# Revit family: STL22465BR_30_STL22465PTO_30
name_source: partatom
category: Luminárias
units: mm (PartAtom-declared; Revit-internal decimal feet)

## family parameters
Com base no plano de trabalho = Não
Compartilhado = Não
Corte com vazios quando carregada = Não
Cota do conector redondo = Utilizar diâmetro
Fonte luminosa = Sim
Manter orientação da anotação = Não
Ponto de cálculo do ambiente = Não
Sempre na vertical = Sim
Tipo de parte = Normal

## types (2) — shared parameters
Altura = 0.05 m
Comprimento = 0.19 m
Cromado = Cromado
Fabricante = Stella
Filtro de cor = 16777215
Fluxo Luminoso = 420 lm
Grau de proteção (IP) = IP20
IRC (Índice de reprodução de cores) = >93 (R9>60)
Largura = 0.04 m
Luminoso = Luminoso - 3000K
Modelo = Trace - Luminária de Luz Pontual
Potência máxima = 7 W
Temperatura da cor (K) = 3000 K
Tensão Elétrica = 100V-240V
Troca de temperatura da cor de lâmpada com esmaecimento = <Nenhum>
URL = https://stella.com.br
Ângulo de Abertura = 40°
Ângulo de inclinação = 90.00°
zero-valued in all types: Elevação padrão

## per-type parameters (varying)
| type | Arquivo de rede fotométrica | Estrutura | Parafuso Branco | Parafuso Preto | Referência |
| STL22465PTO/30 - BIVOLT - 3000K - 420lm - 40° | STELLA - STL22465PTO-30 - TRACE 7W - LUMINÁRIA DE LUZ PONTUAL.ies | Al - Preto | Não | Sim | STL22465PTO/30 - BIVOLT |
| STL22465BR/30 - BIVOLT - 3000K - 420lm - 40° | STELLA - STL22465BR-30 - TRACE 7W - LUMINÁRIA DE LUZ PONTUAL.ies | Al - Branco | Sim | Não | STL22465BR/30 - BIVOLT |
